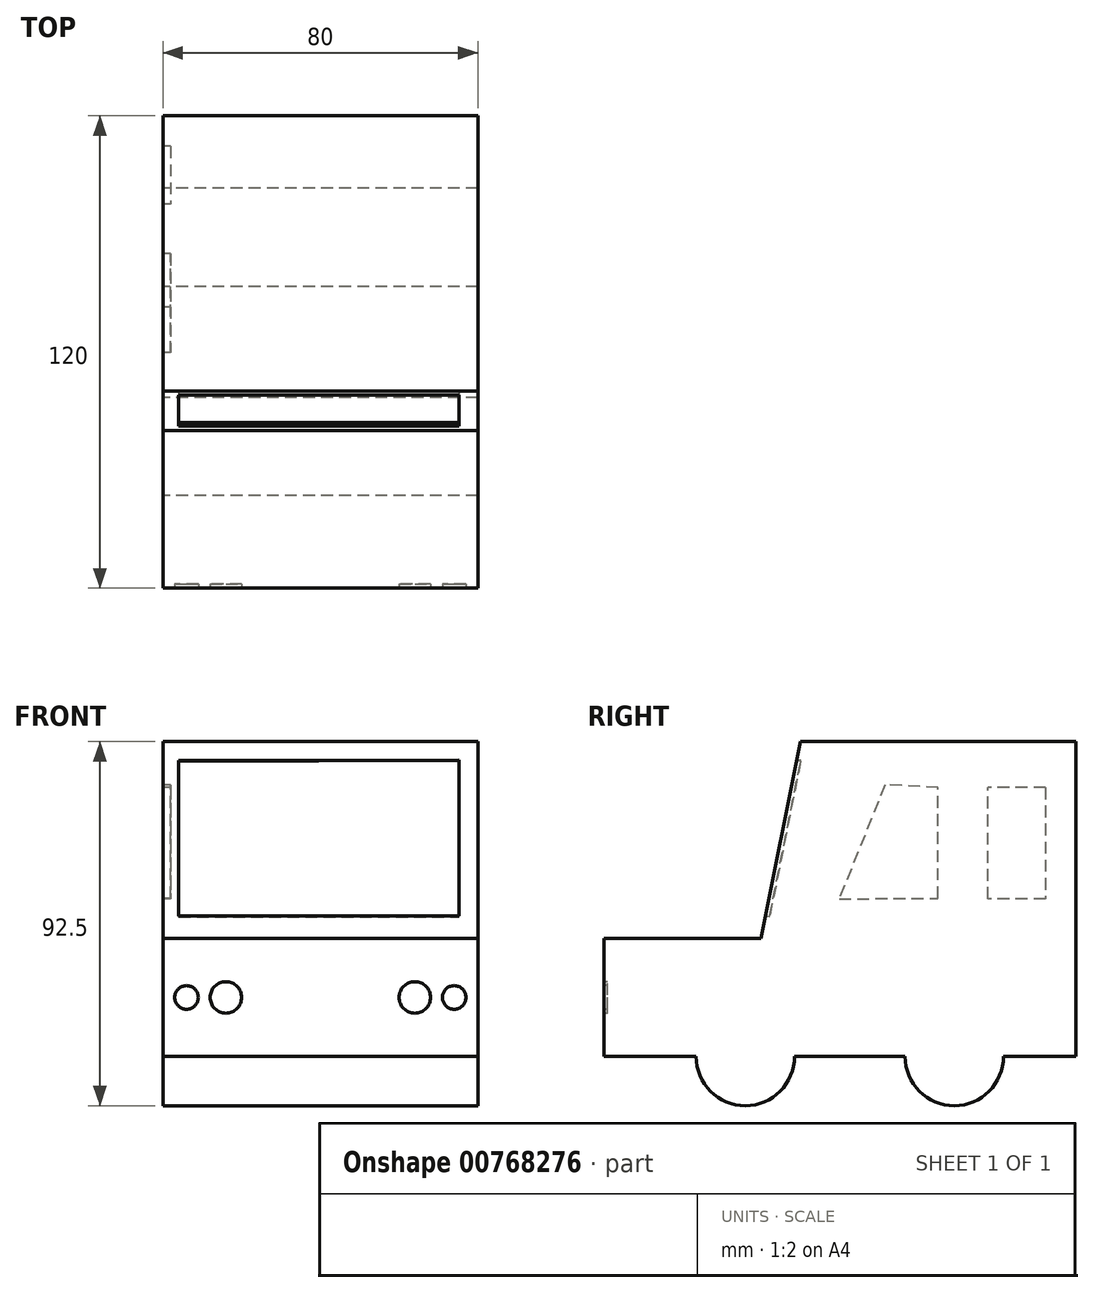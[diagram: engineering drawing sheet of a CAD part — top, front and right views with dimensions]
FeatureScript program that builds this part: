
annotation { "Feature Type Name" : "Feature", "Feature Type Description" : "" }
export const myFeature = defineFeature(function(context is Context, id is Id, definition is map)
    precondition{}
    {
        {
            var Q0;
            Q0=qCreatedBy(makeId("Right.planeOp"),FACE);
            var sketch = newSketch(context, id + "F0", { "sketchPlane" : qUnion([Q0])});
            skLineSegment(sketch, "E0", {"start": v(74.16, 80) * mm, "end": v(74.16, 0) * mm});
            skLineSegment(sketch, "E1", {"start": v(74.16, 0) * mm, "end": v(-45.84, 0) * mm});
            skLineSegment(sketch, "E2", {"start": v(-45.84, 0) * mm, "end": v(-45.84, 30) * mm});
            skLineSegment(sketch, "E3", {"start": v(-45.84, 30) * mm, "end": v(-5.84, 30) * mm});
            skLineSegment(sketch, "E4", {"start": v(74.16, 80) * mm, "end": v(4.16, 80) * mm});
            skLineSegment(sketch, "E5", {"start": v(4.16, 80) * mm, "end": v(-5.84, 30) * mm});
            skCircle(sketch, "E6", {"center": v(-9.88, 0) * mm, "radius": 12.5 * mm});
            skCircle(sketch, "E7", {"center": v(43.22, 0) * mm, "radius": 12.5 * mm});
            skSolve(sketch);
        }
        {
            var Q0;
            Q0 = qSketchRegion(id + "F0", true);
            extrude(context, id + "F1", {"entities" : qUnion([Q0]), "endBound" : BoundingType.SYMMETRIC, "depth" : 80 * mm, "offsetDistance" : 25 * mm});
        }
        {
            var Q0;
            Q0=makeQuery(id+"F1.opExtrude","CAP_FACE",FACE,{"disambiguationData":[OSD([sQuery(id+"F0.wireOp",EDGE,"E0"),sQuery(id+"F0.wireOp",EDGE,"E1"),sQuery(id+"F0.wireOp",EDGE,"E2"),sQuery(id+"F0.wireOp",EDGE,"E3"),sQuery(id+"F0.wireOp",EDGE,"E4"),sQuery(id+"F0.wireOp",EDGE,"E5"),sQuery(id+"F0.wireOp",EDGE,"E6"),sQuery(id+"F0.wireOp",EDGE,"E7")])],"isStart":true});
            var sketch = newSketch(context, id + "F2", { "sketchPlane" : qUnion([Q0])});
            skLineSegment(sketch, "E8", {"start": v(-25.61, 69.02) * mm, "end": v(-13.99, 40.04) * mm});
            skLineSegment(sketch, "E9", {"start": v(-13.99, 40.04) * mm, "end": v(-39.1, 40.2) * mm});
            skLineSegment(sketch, "E10", {"start": v(-39.1, 40.2) * mm, "end": v(-39.1, 68.35) * mm});
            skLineSegment(sketch, "E11", {"start": v(-39.1, 68.35) * mm, "end": v(-25.61, 69.02) * mm});
            skLineSegment(sketch, "E12", {"start": v(-66.4, 68.35) * mm, "end": v(-66.4, 40.04) * mm});
            skLineSegment(sketch, "E13", {"start": v(-66.4, 40.04) * mm, "end": v(-51.74, 40.04) * mm});
            skLineSegment(sketch, "E14", {"start": v(-51.74, 40.04) * mm, "end": v(-51.74, 68.35) * mm});
            skLineSegment(sketch, "E15", {"start": v(-66.4, 68.35) * mm, "end": v(-51.74, 68.35) * mm});
            skLineSegment(sketch, "E16", {"start": v(-51.74, 68.35) * mm, "end": v(-66.4, 68.35) * mm});
            skSolve(sketch);
        }
        {
            var Q0;
            Q0 = qSketchRegion(id + "F2", true);
            extrude(context, id + "F3", {"entities" : qUnion([Q0]), "operationType" : NewBodyOperationType.REMOVE, "oppositeDirection" : true, "depth" : 2 * mm, "offsetDistance" : 25 * mm});
        }
        {
            var Q0;
            Q0=makeQuery(id+"F1.opExtrude","SWEPT_FACE",FACE,{"disambiguationData":[OSD([sQuery(id+"F0.wireOp",EDGE,"E5")])]});
            var sketch = newSketch(context, id + "F4", { "sketchPlane" : qUnion([Q0])});
            skLineSegment(sketch, "E17", {"start": v(-35.98, 74.32) * mm, "end": v(-35.98, 34.06) * mm});
            skLineSegment(sketch, "E18", {"start": v(-35.98, 34.06) * mm, "end": v(35.18, 34.06) * mm});
            skLineSegment(sketch, "E19", {"start": v(35.18, 34.06) * mm, "end": v(35.18, 74.53) * mm});
            skLineSegment(sketch, "E20", {"start": v(-35.98, 74.32) * mm, "end": v(35.18, 74.53) * mm});
            skSolve(sketch);
        }
        {
            var Q0;
            Q0 = qSketchRegion(id + "F4", true);
            extrude(context, id + "F5", {"entities" : qUnion([Q0]), "operationType" : NewBodyOperationType.REMOVE, "endBound" : BoundingType.SYMMETRIC, "oppositeDirection" : true, "depth" : 2 * mm, "offsetDistance" : 25 * mm});
        }
        {
            var Q0;
            Q0=makeQuery(id+"F1.opExtrude","SWEPT_FACE",FACE,{"disambiguationData":[OSD([sQuery(id+"F0.wireOp",EDGE,"E2")])]});
            var sketch = newSketch(context, id + "F6", { "sketchPlane" : qUnion([Q0])});
            skCircle(sketch, "E21", {"center": v(-34, 15) * mm, "radius": 3 * mm});
            skPoint(sketch, "E21.centerSnap0", {"position": v(-40, 15) * mm});
            skCircle(sketch, "E22", {"center": v(-24, 15) * mm, "radius": 4 * mm});
            skCircle(sketch, "E23", {"center": v(24, 15) * mm, "radius": 4 * mm});
            skCircle(sketch, "E24", {"center": v(34, 15) * mm, "radius": 3 * mm});
            skSolve(sketch);
        }
        {
            var Q0;
            Q0 = qSketchRegion(id + "F6", true);
            extrude(context, id + "F7", {"entities" : qUnion([Q0]), "operationType" : NewBodyOperationType.REMOVE, "endBound" : BoundingType.SYMMETRIC, "oppositeDirection" : true, "depth" : 2 * mm, "offsetDistance" : 25 * mm});
        }
    });
